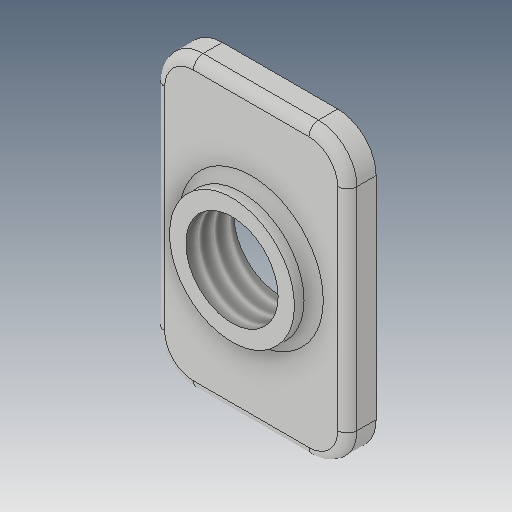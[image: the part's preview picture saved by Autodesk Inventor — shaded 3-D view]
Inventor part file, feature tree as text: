
AUTODESK INVENTOR PART (.ipt)
format: ipt  version: 2017 (Build 210142000, 142)  size: 178,176 bytes
history: native  units: mm
features: other x3, sketch x2
ambient origin geometry x8: Origin, YZ Plane, XZ Plane, XY Plane, X Axis, Y Axis, Z Axis, Center Point
bodies: Solid1 (feature_tree)
feature tree (5):
  other  "M5 Tee Nut-Generic_MIR_CPY_MIR_MIR.ipt"
  other  "Solid1::M5 Tee Nut-Generic_MIR_CPY_MIR_MIR.ipt"
  other  "TaggingFeature1"
  sketch  "Sketch1"  dims[d0=10.0mm]
  sketch  "Sketch2"
